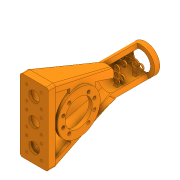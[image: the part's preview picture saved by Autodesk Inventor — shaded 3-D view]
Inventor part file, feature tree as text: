
AUTODESK INVENTOR PART (.ipt)
format: ipt  version: 2020 (Build 240168000, 168)  size: 1,165,824 bytes
history: native  units: in
note: dims shown in document units (in); Inventor stores cm internally (conversion verified against a paired STEP export)
features: chamfer x23, sketch x21, extrude x18, projected_geometry x11, plane x3, loft x2, fillet x1, other x1
ambient origin geometry x8: Origin, YZ Plane, XZ Plane, XY Plane, X Axis, Y Axis, Z Axis, Center Point
bodies: Solid1 (feature_tree)
feature tree (80):
  extrude  "Extrusion1"  Depth=2.0472in
  extrude  "Extrusion2"  Depth=0.2756in
  chamfer  "Chamfer1"  Distance=0.5512in
  extrude  "Extrusion3"  Depth=0.2756in
  extrude  "Extrusion4"  Depth=0.2756in TaperAngle=0.0deg
  extrude  "Extrusion5"  Depth=0.315in
  extrude  "Extrusion6"  Depth=0.4724in
  extrude  "Extrusion7"  Depth=0.0787in
  plane  "Work Plane1"
  extrude  "Extrusion8"  Depth=0.1575in
  plane  "Work Plane2"
  extrude  "Extrusion9"  Depth=1.0994in
  sketch  "Sketch11"  dims[d31=15.0deg d32=0.4921in d33=0.0in]
  plane  "Work Plane3"
  extrude  "Extrusion10"  Depth=0.4921in TaperAngle=0.0deg
  extrude  "Extrusion11"  Depth=1.5748in TaperAngle=360.0deg
  loft  "Loft1"
  loft  "Loft2"
  sketch  "Sketch16"  dims[d47=0.315in d48=0.4331in]
  extrude  "Extrusion12"  Depth=0.0984in TaperAngle=0.0deg
  extrude  "Extrusion13"  Depth=0.4331in
  extrude  "Extrusion14"  Depth=0.6161in
  extrude  "Extrusion15"  Depth=0.1575in
  chamfer  "Chamfer2"  Distance=0.0984in
  chamfer  "Chamfer3"  [1 undecoded]
  chamfer  "Chamfer4"  [1 undecoded]
  chamfer  "Chamfer5"  Distance=1.6654in
  chamfer  "Chamfer6"  Distance=1.6654in
  chamfer  "Chamfer7"  Distance=0.1969in
  chamfer  "Chamfer8"  Distance=0.1969in
  chamfer  "Chamfer9"  Distance=0.3484in
  chamfer  "Chamfer10"  Distance=0.3484in
  chamfer  "Chamfer11"  Distance=0.1969in
  chamfer  "Chamfer12"  Distance=0.1969in
  chamfer  "Chamfer13"  Distance=0.1969in
  chamfer  "Chamfer14"  Distance=0.3937in
  chamfer  "Chamfer15"  Distance=0.7874in
  chamfer  "Chamfer16"  Angle=90.0deg  [1 undecoded]
  chamfer  "Chamfer17"  Angle=90.0deg  [1 undecoded]
  chamfer  "Chamfer18"  Angle=90.0deg  [1 undecoded]
  chamfer  "Chamfer19"  Angle=90.0deg  [1 undecoded]
  chamfer  "Chamfer20"  Distance=0.7874in
  chamfer  "Chamfer21"  Distance=0.3937in
  chamfer  "Chamfer22"  Distance=0.3937in
  fillet  "Fillet1"  Radius=0.7874in
  chamfer  "Chamfer23"  Distance=0.1969in
  extrude  "Extrusion19"  Depth=0.2756in
  extrude  "Extrusion20"  Depth=0.2756in
  extrude  "Extrusion21"  Depth=0.2756in
  sketch  "Sketch1"  dims[d0=2.3622in d1=2.0472in]
  sketch  "Sketch2"  dims[d2=0.2756in d3=0.0in d4=1.6535in d5=0.5512in d6=0.0in]
  sketch  "Sketch3"  dims[d7=0.2756in d8=0.125in d9=0.0137in d10=0.0157in]
  sketch  "Sketch5"  dims[d11=4.7244in d13=360.0deg d15=0.2756in d16=0.0in]
  sketch  "Sketch6"  dims[d17=0.5512in d19=0.315in]
  projected_geometry  "Projected Loop1"
  sketch  "Sketch7"  dims[d20=0.315in d21=0.4724in]
  projected_geometry  "Projected Loop2"
  sketch  "Sketch8"  dims[d22=0.4724in d23=0.0787in d24=0.0787in d25=0.0787in]
  projected_geometry  "Projected Loop3"
  sketch  "Sketch9"  dims[d26=0.0984in d27=0.0in d28=0.1575in]
  sketch  "Sketch10"  dims[d29=0.1575in d30=1.0994in]
  sketch  "Sketch12"  dims[d34=1.4567in d35=0.0in d36=1.5748in d38=360.0deg]
  sketch  "Sketch13"  dims[d40=0.0787in d41=0.0787in]
  projected_geometry  "Projected Loop4"
  other  "Edges1"
  sketch  "Sketch14"  dims[d42=0.0787in d43=0.0787in]
  projected_geometry  "Projected Loop5"
  sketch  "Sketch15"  dims[d44=0.0787in d45=0.0984in d46=0.0in]
  projected_geometry  "Projected Loop6"
  projected_geometry  "Projected Loop7"
  sketch  "Sketch19"  dims[d49=0.0984in d50=0.0in d51=0.6161in]
  projected_geometry  "Projected Loop8"
  sketch  "Sketch20"  dims[d52=0.1575in d53=0.1575in d54=0.0984in d55=0.0in]
  projected_geometry  "Projected Loop9"
  sketch  "Sketch21"  dims[d56=6.6929in]
  sketch  "Sketch25"  dims[d57=0.8858in]
  sketch  "Sketch26"  dims[d58=1.6654in]
  projected_geometry  "Projected Loop11"
  sketch  "Sketch27"  dims[d59=1.6654in d60=0.0in d61=0.0in d62=1.6654in d63=1.6654in d64=0.1969in d65=0.1969in d66=0.3484in d67=0.3484in d68=0.1969in d69=0.1969in d70=0.1969in d71=0.3937in d72=0.0in d73=0.7874in d74=0.0in d75=0.0in d76=90.0deg d77=0.0in d78=90.0deg d79=0.0in d80=90.0deg d81=0.0in d82=90.0deg d86=0.7874in d87=0.0in d90=0.3937in d91=0.3937in d92=0.7874in d93=0.0in d94=0.1969in d95=0.0in d96=0.8858in d97=1.6654in d98=1.6654in d99=0.0in d100=0.0in d101=0.2224in d102=0.1575in d103=0.1575in d104=0.1575in d105=0.1575in d106=0.0984in d107=0.0984in d108=0.1969in d109=0.0in d122=0.1575in d123=0.0787in d124=45.0deg d125=0.0787in d126=0.1575in d127=45.0deg d128=0.1575in d129=0.0787in d130=45.0deg d131=0.0787in d132=0.1575in d133=45.0deg d134=0.1575in d135=0.0787in d136=45.0deg d137=0.1575in d138=0.0787in d139=45.0deg d140=0.1575in d141=0.0787in d142=45.0deg d143=0.1575in d144=0.0787in d145=45.0deg d146=0.0787in d147=0.1575in d148=45.0deg d149=0.1575in d150=0.0787in d151=45.0deg d152=0.1575in d153=0.0787in d154=45.0deg d155=0.0787in d156=0.1575in d157=45.0deg d158=0.0591in d159=0.1575in d160=0.0137in d161=0.0591in d162=0.1575in d163=0.0137in d164=0.0591in d165=0.1575in d166=0.0137in d167=0.0591in d168=0.1575in d169=0.0137in d170=0.0591in d171=0.1575in d172=0.0137in d173=0.0591in d174=0.1575in d175=0.0137in d176=0.0591in d177=0.1575in d178=0.0137in d179=0.0591in d180=0.1575in d181=0.0137in d182=0.0591in d183=0.1575in d184=0.0137in d185=0.0197in d193=0.0984in d194=0.3937in d195=0.125in d196=45.0deg d197=0.2756in d198=0.1969in d199=0.0in d200=0.2756in d201=2.7559in d202=0.2756in d203=0.2756in d204=0.2756in d205=0.2756in d206=0.2756in d207=0.2756in d208=0.2756in d209=0.0394in d210=0.2047in d211=0.0in d212=0.1969in d213=0.2756in d214=0.0in]
  projected_geometry  "Projected Loop12"
note: 6 required parameter values undecoded (feature->parameter linkage not recoverable at this tier; creation-order binding heuristic only, values carry confidence <= 0.55)
